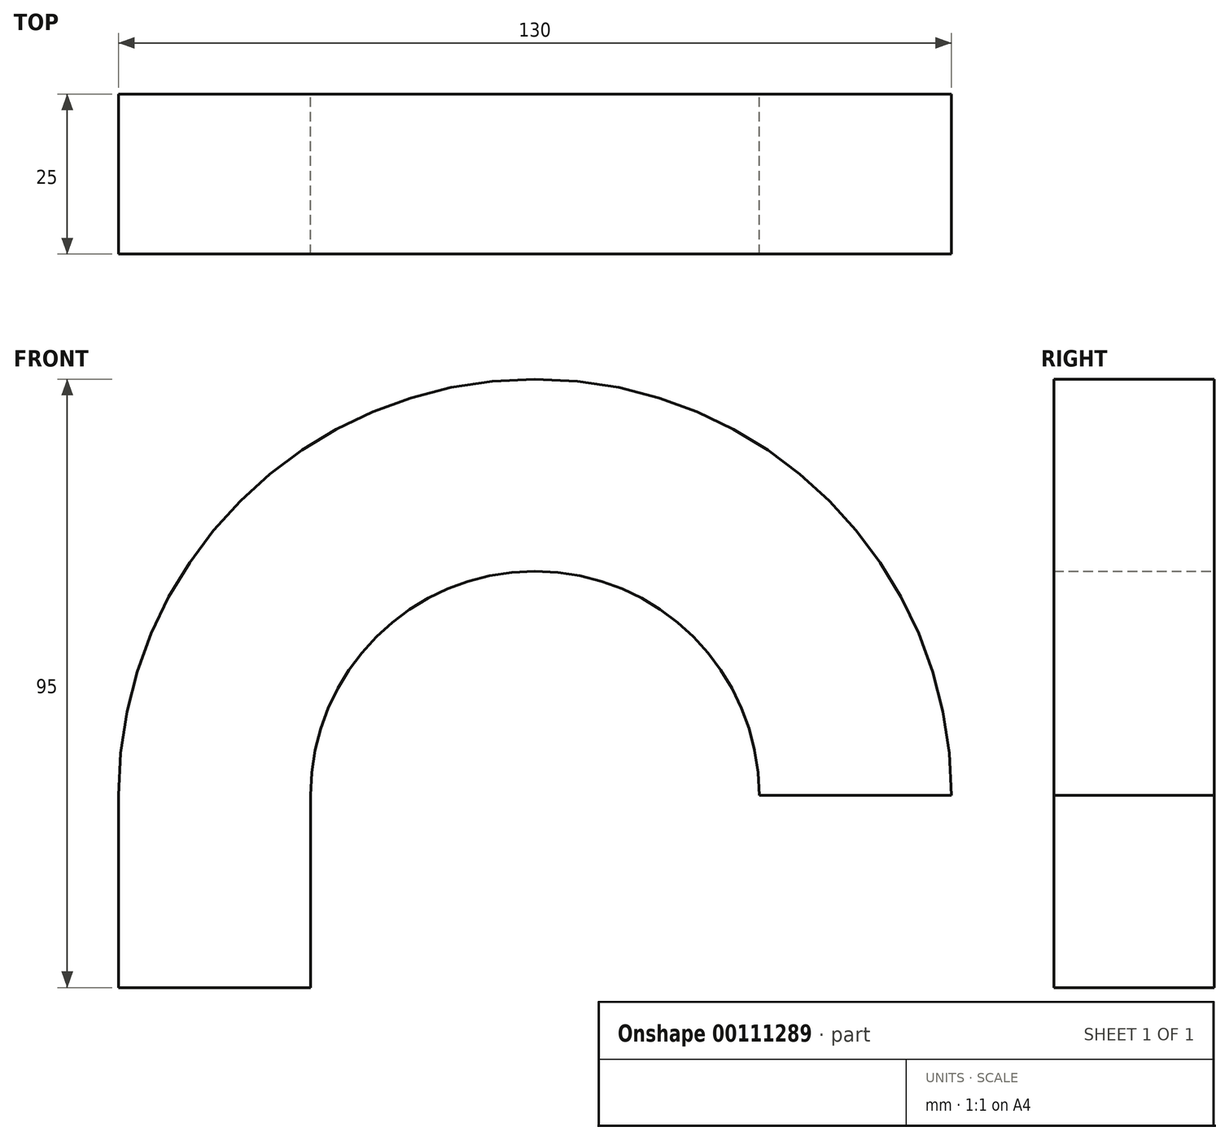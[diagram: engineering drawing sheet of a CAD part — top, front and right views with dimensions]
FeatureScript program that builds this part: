
annotation { "Feature Type Name" : "Feature", "Feature Type Description" : "" }
export const myFeature = defineFeature(function(context is Context, id is Id, definition is map)
    precondition{}
    {
        {
            var Q0;
            Q0=qCreatedBy(makeId("Top.planeOp"),FACE);
            var sketch = newSketch(context, id + "F0", { "sketchPlane" : qUnion([Q0])});
            skLineSegment(sketch, "E0.bottom", {"start": v(15, -12.5) * mm, "end": v(-15, -12.5) * mm});
            skLineSegment(sketch, "E0.top", {"start": v(15, 12.5) * mm, "end": v(-15, 12.5) * mm});
            skLineSegment(sketch, "E0.left", {"start": v(15, -12.5) * mm, "end": v(15, 12.5) * mm});
            skLineSegment(sketch, "E0.right", {"start": v(-15, -12.5) * mm, "end": v(-15, 12.5) * mm});
            skPoint(sketch, "E0.middle", {"position": v(0, 0) * mm});
            skLineSegment(sketch, "E1", {"start": v(0, 0) * mm, "end": v(15, 0) * mm});
            skSolve(sketch);
        }
        {
            var Q0;
            Q0=qCreatedBy(makeId("Front.planeOp"),FACE);
            var sketch = newSketch(context, id + "F1", { "sketchPlane" : qUnion([Q0])});
            skLineSegment(sketch, "E2", {"start": v(0, 0) * mm, "end": v(0, 30) * mm});
            skArc(sketch, "E3", {"start": v(100, 30) * mm, "mid": v(50, 80) * mm, "end": v(0, 30) * mm});
            skSolve(sketch);
        }
        {
            var Q0;
            {var subQ3=sQuery(id+"F0.wireOp",EDGE,"E0.bottom");Q0=makeQuery(id+"F0.imprint","IMPRINT",FACE,{"disambiguationData":[TD([[makeQuery(id+"F0.imprint","IMPRINT",EDGE,{"derivedFrom":subQ3}),-1.0]])]});}
            var Q1;
            Q1=sQuery(id+"F1.wireOp",EDGE,"E2");
            var Q2;
            Q2=sQuery(id+"F1.wireOp",EDGE,"E3");
            sweep(context, id + "F2", {"profiles" : qUnion([Q0]), "path" : qUnion([Q1, Q2])});
        }
    });
